# Revit family: QF_BOURGEAT_Chariots_de_stockage_assiette_ garnies_modulables
name_source: partatom
category: Equipement spécialisé
revit_build: Autodesk Revit 2015 (Build: 20140606_1530(x64)
units: mm (PartAtom-declared; Revit-internal decimal feet)

## types (2) — shared parameters
Fabricant = BOURGEAT
Largeur cage = 660 mm  [stored 2.16535 ft]
Longueur Cadre = 662 mm
Longueur hors tout = 700 mm  [stored 2.29659 ft]
Profondeur hors tout = 700 mm  [stored 2.29659 ft]
Spécification du Fabricant = Chariots modulables pour stockage d'assiettes garnies
URL catalogue = http://www.bourgeat.fr

## per-type parameters (varying)
| type | Charge max | Hauteur hors tout | Hauteur poignée | Modèle | Poids net à vide | Structure intermédiaire |
| Petit modèle | 75.00 kg | 1030 mm  [stored 3.37927 ft] | 807 mm | 798848 | 23.00 kg | Non |
| Grand modèle | 150.00 kg | 1830 mm  [stored 6.00394 ft] | 1607 mm | 798896 | 33.00 kg | Oui |

note: [stored X ft] marks values corroborated as IEEE doubles in the binary element streams (Revit-internal decimal feet)
